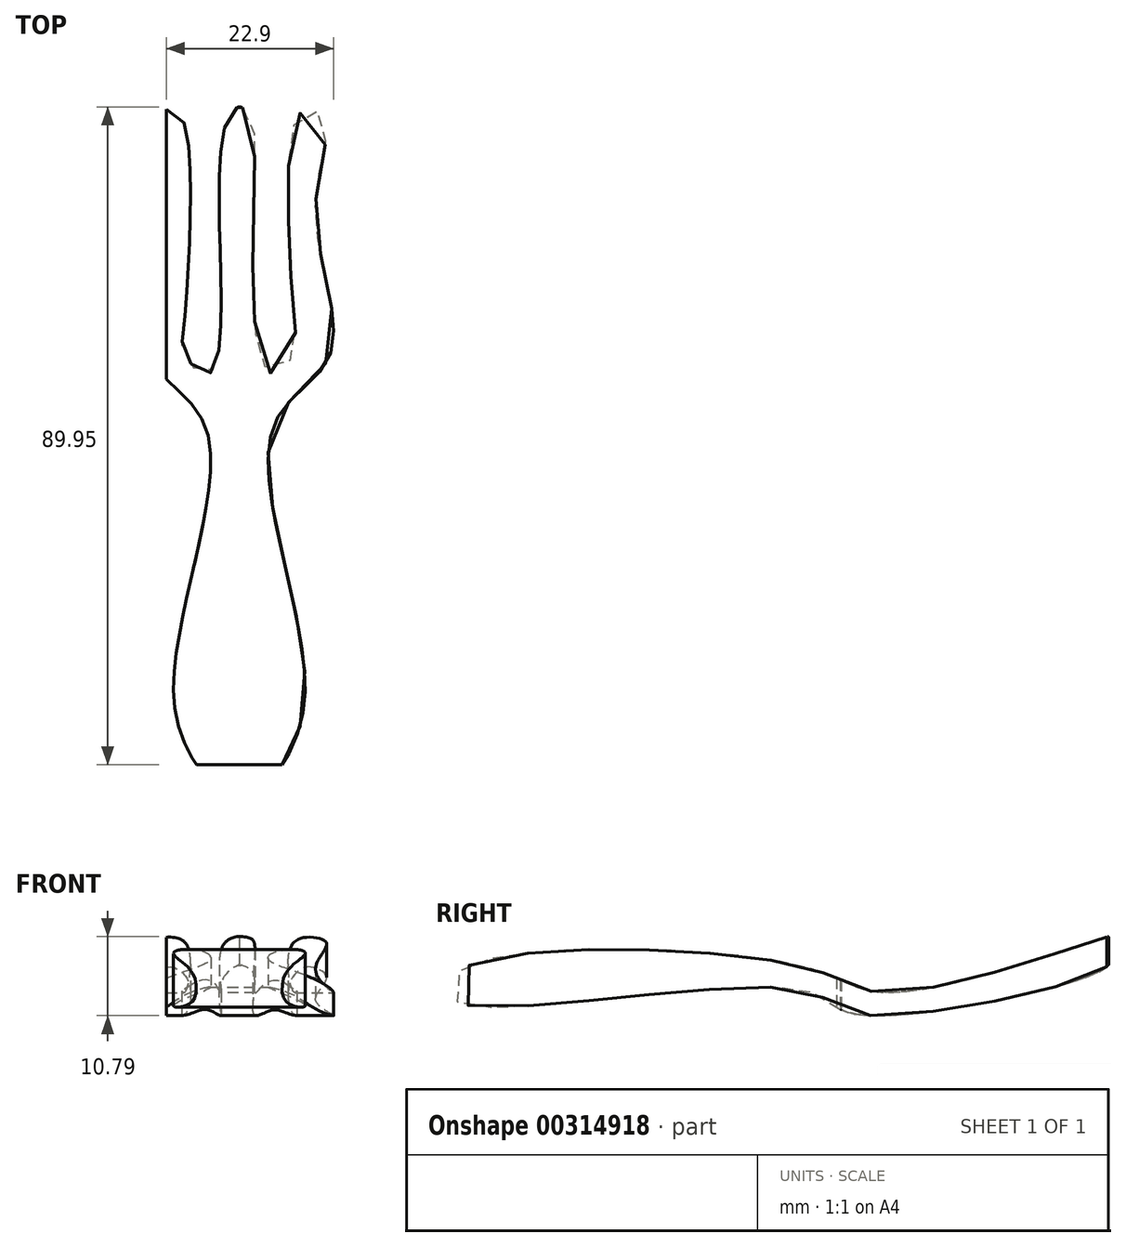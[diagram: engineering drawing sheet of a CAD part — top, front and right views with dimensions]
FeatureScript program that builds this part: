
annotation { "Feature Type Name" : "Feature", "Feature Type Description" : "" }
export const myFeature = defineFeature(function(context is Context, id is Id, definition is map)
    precondition{}
    {
        {
            var Q0;
            Q0=qCreatedBy(makeId("Top.planeOp"),FACE);
            var sketch = newSketch(context, id + "F0", { "sketchPlane" : qUnion([Q0])});
            skLineSegment(sketch, "E0.bottom", {"start": v(15, 50) * mm, "end": v(-15, 50) * mm});
            skLineSegment(sketch, "E0.top", {"start": v(15, -50) * mm, "end": v(-15, -50) * mm});
            skLineSegment(sketch, "E0.left", {"start": v(15, 50) * mm, "end": v(15, -50) * mm});
            skLineSegment(sketch, "E0.right", {"start": v(-15, 50) * mm, "end": v(-15, -50) * mm});
            skPoint(sketch, "E0.middle", {"position": v(0, 0) * mm});
            skSolve(sketch);
        }
        {
            var Q0;
            Q0=makeQuery(id+"F0.imprint","IMPRINT",FACE,{"disambiguationData":[TD([[makeQuery(id+"F0.imprint","IMPRINT",EDGE,{"derivedFrom":sQuery(id+"F0.wireOp",EDGE,"E0.bottom")}),1.0]])]});
            extrude(context, id + "F1", {"entities" : qUnion([Q0]), "depth" : 30 * mm});
        }
        {
            var Q0;
            Q0=makeQuery(id+"F1.opExtrude","CAP_FACE",FACE,{"disambiguationData":[OSD([sQuery(id+"F0.wireOp",EDGE,"E0.bottom"),sQuery(id+"F0.wireOp",EDGE,"E0.top"),sQuery(id+"F0.wireOp",EDGE,"E0.left"),sQuery(id+"F0.wireOp",EDGE,"E0.right")])],"isStart":true});
            var sketch = newSketch(context, id + "F2", { "sketchPlane" : qUnion([Q0])});
            skPoint(sketch, "E1.0.internal.snap0", {"position": v(0, -50) * mm});
            skFitSpline(sketch, "E1", {"points": [v(0, -46.68) * mm, v(2.12, -42.38) * mm, v(2.98, -12.31) * mm, v(5.55, -10.3) * mm, v(7.84, -14.03) * mm, v(7.84, -14.32) * mm, v(7.27, -43.53) * mm, v(9.85, -46.4) * mm, v(11.85, -44.39) * mm, v(10.42, -32.07) * mm, v(12.43, -12.89) * mm, v(4.4, -2.3) * mm, v(8.99, 33.5) * mm, v(0, 50) * mm], "startDerivative": vector(107.69, 15.12) * mm, "endDerivative": vector(-130.58, 132.16) * mm});
            skFitSpline(sketch, "E2.MirrorCS", {"points": [v(0, -46.68) * mm, v(-2.98, -12.31) * mm, v(-5.55, -10.3) * mm, v(-7.84, -14.03) * mm, v(-7.84, -14.32) * mm, v(-7.27, -43.53) * mm, v(-9.85, -46.4) * mm, v(-11.85, -44.39) * mm, v(-10.42, -32.07) * mm, v(-12.43, -12.89) * mm, v(-4.4, -2.3) * mm, v(-8.99, 33.5) * mm, v(0, 50) * mm], "startDerivative": vector(-107.69, 15.12) * mm, "endDerivative": vector(130.58, 132.16) * mm});
            skLineSegment(sketch, "E3", {"start": v(-4.57, 45.37) * mm, "end": v(4.39, 45.25) * mm});
            skSolve(sketch);
        }
        {
            var Q0;
            Q0=makeQuery(id+"F1.opExtrude","SWEPT_FACE",FACE,{"disambiguationData":[OSD([sQuery(id+"F0.wireOp",EDGE,"E0.left")])]});
            var sketch = newSketch(context, id + "F3", { "sketchPlane" : qUnion([Q0])});
            skLineSegment(sketch, "E4.bottom", {"start": v(0, 30) * mm, "end": v(0, 30) * mm});
            skLineSegment(sketch, "E4.top", {"start": v(0, -30) * mm, "end": v(0, -30) * mm});
            skLineSegment(sketch, "E4.left", {"start": v(0, 30) * mm, "end": v(0, -30) * mm, "construction": true});
            skLineSegment(sketch, "E4.right", {"start": v(0, 30) * mm, "end": v(0, -30) * mm, "construction": true});
            skPoint(sketch, "E4.middle", {"position": v(0, 0) * mm});
            skLineSegment(sketch, "E5.bottom", {"start": v(46.6, 6.34) * mm, "end": v(-46.6, 6.34) * mm, "construction": true});
            skLineSegment(sketch, "E5.top", {"start": v(46.6, 24.55) * mm, "end": v(-46.6, 24.55) * mm, "construction": true});
            skLineSegment(sketch, "E5.left", {"start": v(46.6, 6.34) * mm, "end": v(46.6, 24.55) * mm, "construction": true});
            skLineSegment(sketch, "E5.right", {"start": v(-46.6, 6.34) * mm, "end": v(-46.6, 24.55) * mm, "construction": true});
            skPoint(sketch, "E5.middle", {"position": v(0, 15.45) * mm});
            skPoint(sketch, "E6.2.internal.snap0", {"position": v(46.6, 15.45) * mm});
            skPoint(sketch, "E6.3.internal.snap0", {"position": v(46.6, 15.45) * mm});
            skPoint(sketch, "E6.9.internal.snap0", {"position": v(46.6, 15.45) * mm});
            skFitSpline(sketch, "E6", {"points": [v(46.6, 19.4) * mm, v(15.33, 11.8) * mm, v(4.4, 15.45) * mm, v(-40.82, 15.45) * mm, v(-43.25, 12.1) * mm, v(-40.82, 9.98) * mm, v(5, 12.1) * mm, v(12.3, 8.77) * mm, v(46.6, 15.45) * mm, v(45.69, 15.97) * mm], "startDerivative": vector(-243.46, -79.12) * mm, "endDerivative": vector(-108.32, -33.76) * mm});
            skFitSpline(sketch, "E7", {"points": [v(46.6, 19.4) * mm, v(48.5, 18.77) * mm, v(46.6, 15.45) * mm], "startDerivative": vector(6.17, -0.59) * mm, "endDerivative": vector(-5.54, -6.96) * mm});
            skPoint(sketch, "E8", {"position": v(46.54, 15.4) * mm});
            skPoint(sketch, "E9", {"position": v(46.48, 15.33) * mm});
            skSolve(sketch);
        }
        {
            var Q0;
            Q0 = qSketchRegion(id + "F2", true);
            extrude(context, id + "F4", {"entities" : qUnion([Q0]), "operationType" : NewBodyOperationType.INTERSECT, "oppositeDirection" : true, "depth" : 25 * mm});
        }
        {
            var Q0;
            Q0 = qSketchRegion(id + "F3", true);
            extrude(context, id + "F5", {"entities" : qUnion([Q0]), "operationType" : NewBodyOperationType.INTERSECT, "oppositeDirection" : true, "depth" : 25 * mm});
        }
    });
